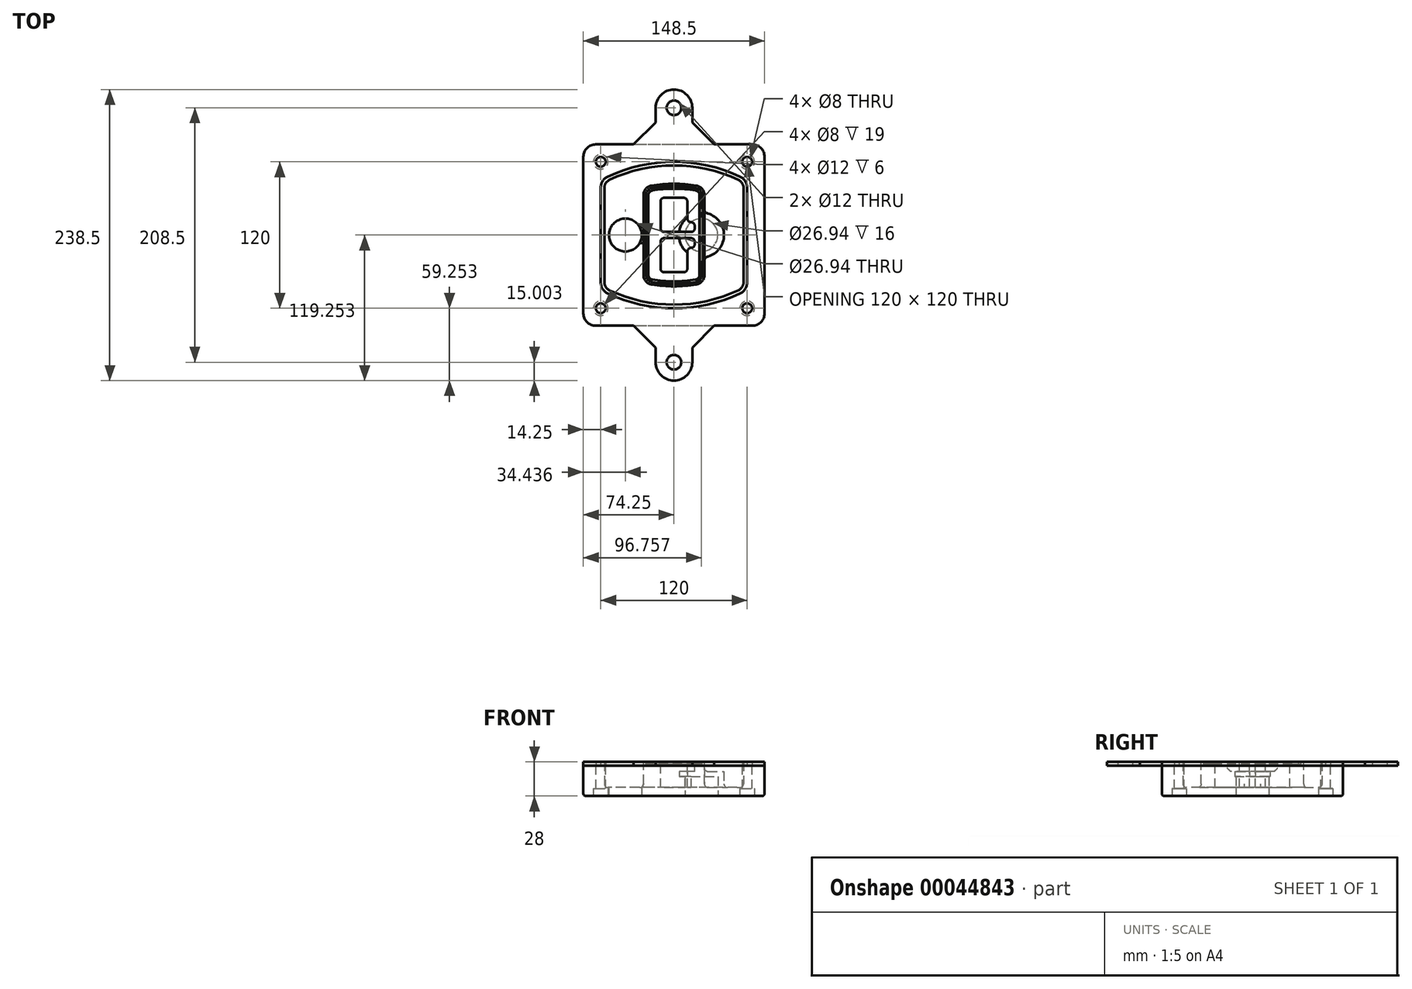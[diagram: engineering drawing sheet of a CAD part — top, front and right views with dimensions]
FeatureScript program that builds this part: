
annotation { "Feature Type Name" : "Feature", "Feature Type Description" : "" }
export const myFeature = defineFeature(function(context is Context, id is Id, definition is map)
    precondition{}
    {
        {
            var Q0;
            Q0=qCreatedBy(makeId("Top.planeOp"),FACE);
            var sketch = newSketch(context, id + "F0", { "sketchPlane" : qUnion([Q0])});
            skPoint(sketch, "E0.rect.middle", {"position": v(0, 0) * mm});
            skLineSegment(sketch, "E1.bottom", {"start": v(24.05, 28.38) * mm, "end": v(152.55, 28.38) * mm});
            skLineSegment(sketch, "E1.top", {"start": v(24.05, 176.88) * mm, "end": v(152.55, 176.88) * mm});
            skLineSegment(sketch, "E1.left", {"start": v(14.05, 38.38) * mm, "end": v(14.05, 166.88) * mm});
            skLineSegment(sketch, "E1.right", {"start": v(162.55, 38.38) * mm, "end": v(162.55, 166.88) * mm});
            skLineSegment(sketch, "E2", {"start": v(14.05, 176.88) * mm, "end": v(162.55, 28.38) * mm, "construction": true});
            skLineSegment(sketch, "E3", {"start": v(162.55, 176.88) * mm, "end": v(14.05, 28.38) * mm, "construction": true});
            skCircle(sketch, "E4", {"center": v(28.3, 162.63) * mm, "radius": 4 * mm});
            skCircle(sketch, "E5", {"center": v(148.3, 162.63) * mm, "radius": 4 * mm});
            skCircle(sketch, "E6", {"center": v(148.3, 42.63) * mm, "radius": 4 * mm});
            skCircle(sketch, "E7", {"center": v(28.3, 42.63) * mm, "radius": 4 * mm});
            skLineSegment(sketch, "E8", {"start": v(28.3, 162.63) * mm, "end": v(148.3, 162.63) * mm, "construction": true});
            skLineSegment(sketch, "E9", {"start": v(148.3, 162.63) * mm, "end": v(148.3, 42.63) * mm, "construction": true});
            skLineSegment(sketch, "E10", {"start": v(148.3, 42.63) * mm, "end": v(28.3, 42.63) * mm, "construction": true});
            skLineSegment(sketch, "E11", {"start": v(28.3, 42.63) * mm, "end": v(28.3, 162.63) * mm, "construction": true});
            skLineSegment(sketch, "E12", {"start": v(28.3, 141.46) * mm, "end": v(28.3, 63.8) * mm});
            skLineSegment(sketch, "E13", {"start": v(148.3, 141.46) * mm, "end": v(148.3, 63.8) * mm});
            skArc(sketch, "E14", {"start": v(142.56, 150.51) * mm, "mid": v(88.3, 162.63) * mm, "end": v(34.04, 150.51) * mm});
            skArc(sketch, "E15", {"start": v(34.04, 54.75) * mm, "mid": v(88.3, 42.63) * mm, "end": v(142.56, 54.75) * mm});
            skLineSegment(sketch, "E16", {"start": v(28.3, 102.63) * mm, "end": v(148.3, 102.63) * mm, "construction": true});
            skPoint(sketch, "E17.visualSharp", {"position": v(28.3, 57.63) * mm});
            skArc(sketch, "E17.filletArc", {"start": v(28.3, 63.8) * mm, "mid": v(29.86, 58.44) * mm, "end": v(34.04, 54.75) * mm});
            skPoint(sketch, "E18.visualSharp", {"position": v(28.3, 147.63) * mm});
            skArc(sketch, "E18.filletArc", {"start": v(34.04, 150.51) * mm, "mid": v(29.86, 146.82) * mm, "end": v(28.3, 141.46) * mm});
            skPoint(sketch, "E19.visualSharp", {"position": v(148.3, 147.63) * mm});
            skArc(sketch, "E19.filletArc", {"start": v(148.3, 141.46) * mm, "mid": v(146.74, 146.82) * mm, "end": v(142.56, 150.51) * mm});
            skPoint(sketch, "E20.visualSharp", {"position": v(148.3, 57.63) * mm});
            skArc(sketch, "E20.filletArc", {"start": v(142.56, 54.75) * mm, "mid": v(146.74, 58.44) * mm, "end": v(148.3, 63.8) * mm});
            skPoint(sketch, "E21.visualSharp", {"position": v(14.05, 176.88) * mm});
            skArc(sketch, "E21.filletArc", {"start": v(24.05, 176.88) * mm, "mid": v(16.98, 173.95) * mm, "end": v(14.05, 166.88) * mm});
            skPoint(sketch, "E22.visualSharp", {"position": v(162.55, 176.88) * mm});
            skArc(sketch, "E22.filletArc", {"start": v(162.55, 166.88) * mm, "mid": v(159.62, 173.95) * mm, "end": v(152.55, 176.88) * mm});
            skPoint(sketch, "E23.visualSharp", {"position": v(162.55, 28.38) * mm});
            skArc(sketch, "E23.filletArc", {"start": v(152.55, 28.38) * mm, "mid": v(159.62, 31.31) * mm, "end": v(162.55, 38.38) * mm});
            skPoint(sketch, "E24.visualSharp", {"position": v(14.05, 28.38) * mm});
            skArc(sketch, "E24.filletArc", {"start": v(14.05, 38.38) * mm, "mid": v(16.98, 31.31) * mm, "end": v(24.05, 28.38) * mm});
            skArc(sketch, "E25.0", {"start": v(145.3, 141.46) * mm, "mid": v(144.2, 145.22) * mm, "end": v(141.28, 147.8) * mm});
            skLineSegment(sketch, "E25.1", {"start": v(145.3, 141.46) * mm, "end": v(145.3, 63.8) * mm});
            skArc(sketch, "E25.2", {"start": v(141.28, 57.47) * mm, "mid": v(144.2, 60.05) * mm, "end": v(145.3, 63.8) * mm});
            skArc(sketch, "E25.3", {"start": v(35.32, 57.47) * mm, "mid": v(88.3, 45.63) * mm, "end": v(141.28, 57.47) * mm});
            skArc(sketch, "E25.4", {"start": v(31.3, 63.8) * mm, "mid": v(32.4, 60.05) * mm, "end": v(35.32, 57.47) * mm});
            skArc(sketch, "E25.5", {"start": v(141.28, 147.8) * mm, "mid": v(88.3, 159.63) * mm, "end": v(35.32, 147.8) * mm});
            skLineSegment(sketch, "E25.6", {"start": v(31.3, 141.46) * mm, "end": v(31.3, 63.8) * mm});
            skArc(sketch, "E25.7", {"start": v(35.32, 147.8) * mm, "mid": v(32.4, 145.22) * mm, "end": v(31.3, 141.46) * mm});
            skArc(sketch, "E26.0", {"start": v(32.34, 154.13) * mm, "mid": v(26.48, 148.97) * mm, "end": v(24.3, 141.46) * mm});
            skArc(sketch, "E26.1", {"start": v(144.26, 154.13) * mm, "mid": v(88.3, 166.63) * mm, "end": v(32.34, 154.13) * mm});
            skArc(sketch, "E26.2", {"start": v(152.3, 141.46) * mm, "mid": v(150.12, 148.97) * mm, "end": v(144.26, 154.13) * mm});
            skLineSegment(sketch, "E26.3", {"start": v(152.3, 141.46) * mm, "end": v(152.3, 63.8) * mm});
            skArc(sketch, "E26.4", {"start": v(144.26, 51.13) * mm, "mid": v(150.12, 56.3) * mm, "end": v(152.3, 63.8) * mm});
            skLineSegment(sketch, "E26.5", {"start": v(24.3, 141.46) * mm, "end": v(24.3, 63.8) * mm});
            skArc(sketch, "E26.6", {"start": v(32.34, 51.13) * mm, "mid": v(88.3, 38.63) * mm, "end": v(144.26, 51.13) * mm});
            skArc(sketch, "E26.7", {"start": v(24.3, 63.8) * mm, "mid": v(26.48, 56.3) * mm, "end": v(32.34, 51.13) * mm});
            skSolve(sketch);
        }
        {
            var Q0;
            Q0=makeQuery(id+"F0.imprint","IMPRINT",FACE,{"disambiguationData":[TD([[makeQuery(id+"F0.imprint","IMPRINT",EDGE,{"derivedFrom":sQuery(id+"F0.wireOp",EDGE,"E1.bottom")}),1.0]])]});
            var Q1;
            Q1=makeQuery(id+"F0.imprint","IMPRINT",FACE,{"disambiguationData":[TD([[makeQuery(id+"F0.imprint","IMPRINT",EDGE,{"derivedFrom":sQuery(id+"F0.wireOp",EDGE,"E12")}),1.0]])]});
            var Q2;
            Q2=makeQuery(id+"F0.imprint","IMPRINT",FACE,{"disambiguationData":[TD([[makeQuery(id+"F0.imprint","IMPRINT",EDGE,{"derivedFrom":sQuery(id+"F0.wireOp",EDGE,"E25.0")}),1.0]])]});
            var Q3;
            Q3=makeQuery(id+"F0.imprint","IMPRINT",FACE,{"disambiguationData":[TD([[makeQuery(id+"F0.imprint","IMPRINT",EDGE,{"derivedFrom":sQuery(id+"F0.wireOp",EDGE,"E12")}),-1.0]])]});
            extrude(context, id + "F1", {"entities" : qUnion([Q0, Q1, Q2, Q3]), "oppositeDirection" : true, "depth" : 25 * mm});
        }
        {
            var Q0;
            Q0=makeQuery(id+"F0.imprint","IMPRINT",FACE,{"disambiguationData":[TD([[makeQuery(id+"F0.imprint","IMPRINT",EDGE,{"derivedFrom":sQuery(id+"F0.wireOp",EDGE,"E12")}),1.0]])]});
            extrude(context, id + "F2", {"entities" : qUnion([Q0]), "operationType" : NewBodyOperationType.ADD, "depth" : 3 * mm});
        }
        {
            var Q0;
            Q0=makeQuery(id+"F0.imprint","IMPRINT",FACE,{"disambiguationData":[TD([[makeQuery(id+"F0.imprint","IMPRINT",EDGE,{"derivedFrom":sQuery(id+"F0.wireOp",EDGE,"E25.0")}),1.0]])]});
            extrude(context, id + "F3", {"entities" : qUnion([Q0]), "operationType" : NewBodyOperationType.REMOVE, "oppositeDirection" : true, "depth" : 18 * mm});
        }
        {
            var Q0;
            Q0=makeQuery(id+"F2.opExtrude","CAP_FACE",FACE,{"disambiguationData":[OSD([sQuery(id+"F0.wireOp",EDGE,"E12"),sQuery(id+"F0.wireOp",EDGE,"E13"),sQuery(id+"F0.wireOp",EDGE,"E14"),sQuery(id+"F0.wireOp",EDGE,"E15"),sQuery(id+"F0.wireOp",EDGE,"E17.filletArc"),sQuery(id+"F0.wireOp",EDGE,"E18.filletArc"),sQuery(id+"F0.wireOp",EDGE,"E19.filletArc"),sQuery(id+"F0.wireOp",EDGE,"E20.filletArc"),sQuery(id+"F0.wireOp",EDGE,"E25.0"),sQuery(id+"F0.wireOp",EDGE,"E25.1"),sQuery(id+"F0.wireOp",EDGE,"E25.2"),sQuery(id+"F0.wireOp",EDGE,"E25.3"),sQuery(id+"F0.wireOp",EDGE,"E25.4"),sQuery(id+"F0.wireOp",EDGE,"E25.5"),sQuery(id+"F0.wireOp",EDGE,"E25.6"),sQuery(id+"F0.wireOp",EDGE,"E25.7")])],"isStart":false});
            var sketch = newSketch(context, id + "F4", { "sketchPlane" : qUnion([Q0])});
            skArc(sketch, "E27.0", {"start": v(69.96, 62.18) * mm, "mid": v(88.3, 60.63) * mm, "end": v(106.64, 62.18) * mm});
            skArc(sketch, "E28.0", {"start": v(106.64, 143.09) * mm, "mid": v(88.3, 144.63) * mm, "end": v(69.96, 143.09) * mm});
            skLineSegment(sketch, "E29", {"start": v(63.3, 135.2) * mm, "end": v(63.3, 70.07) * mm});
            skLineSegment(sketch, "E30", {"start": v(113.3, 135.2) * mm, "end": v(113.3, 70.07) * mm});
            skLineSegment(sketch, "E31", {"start": v(63.3, 141.74) * mm, "end": v(113.3, 141.74) * mm, "construction": true});
            skLineSegment(sketch, "E32", {"start": v(63.3, 63.52) * mm, "end": v(113.3, 63.52) * mm, "construction": true});
            skPoint(sketch, "E33.visualSharp", {"position": v(63.3, 141.74) * mm});
            skArc(sketch, "E33.filletArc", {"start": v(69.96, 143.09) * mm, "mid": v(65.19, 140.36) * mm, "end": v(63.3, 135.2) * mm});
            skPoint(sketch, "E34.visualSharp", {"position": v(113.3, 141.74) * mm});
            skArc(sketch, "E34.filletArc", {"start": v(113.3, 135.2) * mm, "mid": v(111.41, 140.36) * mm, "end": v(106.64, 143.09) * mm});
            skPoint(sketch, "E35.visualSharp", {"position": v(113.3, 63.52) * mm});
            skArc(sketch, "E35.filletArc", {"start": v(106.64, 62.18) * mm, "mid": v(111.41, 64.9) * mm, "end": v(113.3, 70.07) * mm});
            skPoint(sketch, "E36.visualSharp", {"position": v(63.3, 63.52) * mm});
            skArc(sketch, "E36.filletArc", {"start": v(63.3, 70.07) * mm, "mid": v(65.19, 64.9) * mm, "end": v(69.96, 62.18) * mm});
            skArc(sketch, "E37.0", {"start": v(141.28, 147.8) * mm, "mid": v(88.3, 159.63) * mm, "end": v(35.32, 147.8) * mm});
            skArc(sketch, "E37.1", {"start": v(35.32, 147.8) * mm, "mid": v(32.4, 145.22) * mm, "end": v(31.3, 141.46) * mm});
            skLineSegment(sketch, "E37.2", {"start": v(31.3, 141.46) * mm, "end": v(31.3, 63.8) * mm});
            skArc(sketch, "E37.3", {"start": v(31.3, 63.8) * mm, "mid": v(32.4, 60.05) * mm, "end": v(35.32, 57.47) * mm});
            skArc(sketch, "E37.4", {"start": v(35.32, 57.47) * mm, "mid": v(88.3, 45.63) * mm, "end": v(141.28, 57.47) * mm});
            skArc(sketch, "E37.5", {"start": v(141.28, 57.47) * mm, "mid": v(144.2, 60.05) * mm, "end": v(145.3, 63.8) * mm});
            skLineSegment(sketch, "E37.6", {"start": v(145.3, 141.46) * mm, "end": v(145.3, 63.8) * mm});
            skArc(sketch, "E37.7", {"start": v(145.3, 141.46) * mm, "mid": v(144.2, 145.22) * mm, "end": v(141.28, 147.8) * mm});
            skLineSegment(sketch, "E38.0", {"start": v(111.3, 135.2) * mm, "end": v(111.3, 70.07) * mm});
            skArc(sketch, "E38.1", {"start": v(106.3, 64.15) * mm, "mid": v(109.88, 66.2) * mm, "end": v(111.3, 70.07) * mm});
            skArc(sketch, "E38.2", {"start": v(70.3, 64.15) * mm, "mid": v(88.3, 62.63) * mm, "end": v(106.3, 64.15) * mm});
            skArc(sketch, "E38.3", {"start": v(65.3, 70.07) * mm, "mid": v(66.72, 66.2) * mm, "end": v(70.3, 64.15) * mm});
            skLineSegment(sketch, "E38.4", {"start": v(65.3, 135.2) * mm, "end": v(65.3, 70.07) * mm});
            skArc(sketch, "E38.5", {"start": v(111.3, 135.2) * mm, "mid": v(109.88, 139.07) * mm, "end": v(106.3, 141.11) * mm});
            skArc(sketch, "E38.6", {"start": v(70.3, 141.11) * mm, "mid": v(66.72, 139.07) * mm, "end": v(65.3, 135.2) * mm});
            skArc(sketch, "E38.7", {"start": v(106.3, 141.11) * mm, "mid": v(88.3, 142.63) * mm, "end": v(70.3, 141.11) * mm});
            skArc(sketch, "E39.0", {"start": v(109.3, 135.2) * mm, "mid": v(108.36, 137.78) * mm, "end": v(105.97, 139.14) * mm});
            skLineSegment(sketch, "E39.1", {"start": v(109.3, 135.2) * mm, "end": v(109.3, 70.07) * mm});
            skArc(sketch, "E39.2", {"start": v(105.97, 66.12) * mm, "mid": v(108.36, 67.49) * mm, "end": v(109.3, 70.07) * mm});
            skArc(sketch, "E39.3", {"start": v(70.63, 66.12) * mm, "mid": v(88.3, 64.63) * mm, "end": v(105.97, 66.12) * mm});
            skArc(sketch, "E39.4", {"start": v(67.3, 70.07) * mm, "mid": v(68.24, 67.49) * mm, "end": v(70.63, 66.12) * mm});
            skArc(sketch, "E39.5", {"start": v(105.97, 139.14) * mm, "mid": v(88.3, 140.63) * mm, "end": v(70.63, 139.14) * mm});
            skLineSegment(sketch, "E39.6", {"start": v(67.3, 135.2) * mm, "end": v(67.3, 70.07) * mm});
            skArc(sketch, "E39.7", {"start": v(70.63, 139.14) * mm, "mid": v(68.24, 137.78) * mm, "end": v(67.3, 135.2) * mm});
            skLineSegment(sketch, "E40", {"start": v(63.3, 102.63) * mm, "end": v(113.3, 102.63) * mm, "construction": true});
            skLineSegment(sketch, "E41", {"start": v(77.3, 108.13) * mm, "end": v(77.3, 130.13) * mm});
            skLineSegment(sketch, "E42", {"start": v(80.3, 133.13) * mm, "end": v(96.3, 133.13) * mm});
            skLineSegment(sketch, "E43", {"start": v(99.3, 130.13) * mm, "end": v(99.3, 116.13) * mm});
            skLineSegment(sketch, "E44", {"start": v(102.3, 113.13) * mm, "end": v(102.3, 113.13) * mm});
            skLineSegment(sketch, "E45", {"start": v(105.3, 110.13) * mm, "end": v(105.3, 108.13) * mm});
            skLineSegment(sketch, "E46", {"start": v(102.3, 105.13) * mm, "end": v(80.3, 105.13) * mm});
            skPoint(sketch, "E47.visualSharp", {"position": v(77.3, 133.13) * mm});
            skArc(sketch, "E47.filletArc", {"start": v(80.3, 133.13) * mm, "mid": v(78.18, 132.25) * mm, "end": v(77.3, 130.13) * mm});
            skPoint(sketch, "E48.visualSharp", {"position": v(99.3, 133.13) * mm});
            skArc(sketch, "E48.filletArc", {"start": v(99.3, 130.13) * mm, "mid": v(98.42, 132.25) * mm, "end": v(96.3, 133.13) * mm});
            skPoint(sketch, "E49.visualSharp", {"position": v(99.3, 113.13) * mm});
            skArc(sketch, "E49.filletArc", {"start": v(99.3, 116.13) * mm, "mid": v(100.18, 114.01) * mm, "end": v(102.3, 113.13) * mm});
            skPoint(sketch, "E50.visualSharp", {"position": v(105.3, 113.13) * mm});
            skArc(sketch, "E50.filletArc", {"start": v(105.3, 110.13) * mm, "mid": v(104.42, 112.25) * mm, "end": v(102.3, 113.13) * mm});
            skPoint(sketch, "E51.visualSharp", {"position": v(105.3, 105.13) * mm});
            skArc(sketch, "E51.filletArc", {"start": v(102.3, 105.13) * mm, "mid": v(104.42, 106.01) * mm, "end": v(105.3, 108.13) * mm});
            skPoint(sketch, "E52.visualSharp", {"position": v(77.3, 105.13) * mm});
            skArc(sketch, "E52.filletArc", {"start": v(77.3, 108.13) * mm, "mid": v(78.18, 106.01) * mm, "end": v(80.3, 105.13) * mm});
            skLineSegment(sketch, "E53.0.MirrorCS", {"start": v(102.3, 100.13) * mm, "end": v(80.3, 100.13) * mm});
            skArc(sketch, "E54.0.MirrorCS", {"start": v(77.3, 97.13) * mm, "mid": v(78.18, 99.25) * mm, "end": v(80.3, 100.13) * mm});
            skLineSegment(sketch, "E55.0.MirrorCS", {"start": v(77.3, 97.13) * mm, "end": v(77.3, 75.13) * mm});
            skArc(sketch, "E56.0.MirrorCS", {"start": v(80.3, 72.13) * mm, "mid": v(78.18, 73.01) * mm, "end": v(77.3, 75.13) * mm});
            skLineSegment(sketch, "E57.0.MirrorCS", {"start": v(80.3, 72.13) * mm, "end": v(96.3, 72.13) * mm});
            skArc(sketch, "E58.0.MirrorCS", {"start": v(99.3, 75.13) * mm, "mid": v(98.42, 73.01) * mm, "end": v(96.3, 72.13) * mm});
            skLineSegment(sketch, "E59.0.MirrorCS", {"start": v(99.3, 75.13) * mm, "end": v(99.3, 89.13) * mm});
            skArc(sketch, "E60.0.MirrorCS", {"start": v(99.3, 89.13) * mm, "mid": v(100.18, 91.25) * mm, "end": v(102.3, 92.13) * mm});
            skArc(sketch, "E61.0.MirrorCS", {"start": v(105.3, 95.13) * mm, "mid": v(104.42, 93.01) * mm, "end": v(102.3, 92.13) * mm});
            skLineSegment(sketch, "E62.0.MirrorCS", {"start": v(105.3, 95.13) * mm, "end": v(105.3, 97.13) * mm});
            skArc(sketch, "E63.0.MirrorCS", {"start": v(102.3, 100.13) * mm, "mid": v(104.42, 99.25) * mm, "end": v(105.3, 97.13) * mm});
            skSolve(sketch);
        }
        {
            var Q0;
            Q0=makeQuery(id+"F4.imprint","IMPRINT",FACE,{"disambiguationData":[TD([[makeQuery(id+"F4.imprint","IMPRINT",EDGE,{"derivedFrom":sQuery(id+"F4.wireOp",EDGE,"E27.0")}),1.0]])]});
            var Q1;
            Q1=makeQuery(id+"F4.imprint","IMPRINT",FACE,{"disambiguationData":[TD([[makeQuery(id+"F4.imprint","IMPRINT",EDGE,{"derivedFrom":sQuery(id+"F4.wireOp",EDGE,"E38.0")}),-1.0]])]});
            var Q2;
            Q2=makeQuery(id+"F4.imprint","IMPRINT",FACE,{"disambiguationData":[TD([[makeQuery(id+"F4.imprint","IMPRINT",EDGE,{"derivedFrom":sQuery(id+"F4.wireOp",EDGE,"E39.0")}),1.0]])]});
            extrude(context, id + "F5", {"entities" : qUnion([Q0, Q1, Q2]), "operationType" : NewBodyOperationType.ADD, "endBound" : BoundingType.UP_TO_NEXT, "oppositeDirection" : true, "depth" : 25 * mm});
        }
        {
            var Q0;
            Q0=makeQuery(id+"F4.imprint","IMPRINT",FACE,{"disambiguationData":[TD([[makeQuery(id+"F4.imprint","IMPRINT",EDGE,{"derivedFrom":sQuery(id+"F4.wireOp",EDGE,"E38.0")}),-1.0]])]});
            extrude(context, id + "F6", {"entities" : qUnion([Q0]), "operationType" : NewBodyOperationType.REMOVE, "oppositeDirection" : true, "depth" : 2 * mm});
        }
        {
            var Q0;
            Q0=makeQuery(id+"F1.opExtrude","CAP_FACE",FACE,{"disambiguationData":[OSD([sQuery(id+"F0.wireOp",EDGE,"E1.bottom"),sQuery(id+"F0.wireOp",EDGE,"E1.top"),sQuery(id+"F0.wireOp",EDGE,"E1.left"),sQuery(id+"F0.wireOp",EDGE,"E1.right"),sQuery(id+"F0.wireOp",EDGE,"E4"),sQuery(id+"F0.wireOp",EDGE,"E5"),sQuery(id+"F0.wireOp",EDGE,"E6"),sQuery(id+"F0.wireOp",EDGE,"E7"),sQuery(id+"F0.wireOp",EDGE,"E21.filletArc"),sQuery(id+"F0.wireOp",EDGE,"E22.filletArc"),sQuery(id+"F0.wireOp",EDGE,"E23.filletArc"),sQuery(id+"F0.wireOp",EDGE,"E24.filletArc")])],"isStart":false});
            var sketch = newSketch(context, id + "F7", { "sketchPlane" : qUnion([Q0])});
            skCircle(sketch, "E64", {"center": v(110.8, -102.63) * mm, "radius": 13.47 * mm});
            skCircle(sketch, "E65", {"center": v(48.49, -102.63) * mm, "radius": 13.47 * mm});
            skLineSegment(sketch, "E66", {"start": v(162.55, -102.63) * mm, "end": v(14.05, -102.63) * mm});
            skCircle(sketch, "E67", {"center": v(110.8, -102.63) * mm, "radius": 18.47 * mm});
            skCircle(sketch, "E68", {"center": v(148.3, -162.63) * mm, "radius": 6 * mm});
            skCircle(sketch, "E69", {"center": v(28.3, -162.63) * mm, "radius": 6 * mm});
            skCircle(sketch, "E70", {"center": v(28.3, -42.63) * mm, "radius": 6 * mm});
            skCircle(sketch, "E71", {"center": v(148.3, -42.63) * mm, "radius": 6 * mm});
            skSolve(sketch);
        }
        {
            var Q0;
            {var subQ1=sQuery(id+"F7.wireOp",EDGE,"E66");var subQ4=sQuery(id+"F7.wireOp",EDGE,"E64");var subQ6=makeQuery(id+"F7.imprint","INTERSECT",VERTEX,{"disambiguationData":[OD(0.0)],"derivedFrom":[subQ4,subQ1]});Q0=makeQuery(id+"F7.imprint","IMPRINT",FACE,{"disambiguationData":[TD([[makeQuery(id+"F7.imprint","IMPRINT",EDGE,{"disambiguationData":[TD([[subQ6,-1.0]])],"derivedFrom":subQ4}),-1.0]])]});}
            var Q1;
            {var subQ0=sQuery(id+"F7.wireOp",EDGE,"E66");var subQ1=sQuery(id+"F7.wireOp",EDGE,"E64");var subQ3=makeQuery(id+"F7.imprint","INTERSECT",VERTEX,{"disambiguationData":[OD(0.0)],"derivedFrom":[subQ1,subQ0]});Q1=makeQuery(id+"F7.imprint","IMPRINT",FACE,{"disambiguationData":[TD([[makeQuery(id+"F7.imprint","IMPRINT",EDGE,{"disambiguationData":[TD([[subQ3,-1.0]])],"derivedFrom":subQ1}),1.0]])]});}
            var Q2;
            {var subQ0=sQuery(id+"F7.wireOp",EDGE,"E66");var subQ1=sQuery(id+"F7.wireOp",EDGE,"E64");var subQ3=makeQuery(id+"F7.imprint","INTERSECT",VERTEX,{"disambiguationData":[OD(0.0)],"derivedFrom":[subQ1,subQ0]});Q2=makeQuery(id+"F7.imprint","IMPRINT",FACE,{"disambiguationData":[TD([[makeQuery(id+"F7.imprint","IMPRINT",EDGE,{"disambiguationData":[TD([[subQ3,1.0]])],"derivedFrom":subQ1}),1.0]])]});}
            var Q3;
            {var subQ1=sQuery(id+"F7.wireOp",EDGE,"E66");var subQ4=sQuery(id+"F7.wireOp",EDGE,"E64");var subQ6=makeQuery(id+"F7.imprint","INTERSECT",VERTEX,{"disambiguationData":[OD(0.0)],"derivedFrom":[subQ4,subQ1]});Q3=makeQuery(id+"F7.imprint","IMPRINT",FACE,{"disambiguationData":[TD([[makeQuery(id+"F7.imprint","IMPRINT",EDGE,{"disambiguationData":[TD([[subQ6,1.0]])],"derivedFrom":subQ4}),-1.0]])]});}
            extrude(context, id + "F8", {"entities" : qUnion([Q0, Q1, Q2, Q3]), "operationType" : NewBodyOperationType.ADD, "oppositeDirection" : true, "depth" : 20 * mm});
        }
        {
            var Q0;
            {var subQ0=sQuery(id+"F7.wireOp",EDGE,"E66");var subQ1=sQuery(id+"F7.wireOp",EDGE,"E64");var subQ3=makeQuery(id+"F7.imprint","INTERSECT",VERTEX,{"disambiguationData":[OD(0.0)],"derivedFrom":[subQ1,subQ0]});Q0=makeQuery(id+"F7.imprint","IMPRINT",FACE,{"disambiguationData":[TD([[makeQuery(id+"F7.imprint","IMPRINT",EDGE,{"disambiguationData":[TD([[subQ3,-1.0]])],"derivedFrom":subQ1}),1.0]])]});}
            var Q1;
            {var subQ0=sQuery(id+"F7.wireOp",EDGE,"E66");var subQ1=sQuery(id+"F7.wireOp",EDGE,"E64");var subQ3=makeQuery(id+"F7.imprint","INTERSECT",VERTEX,{"disambiguationData":[OD(0.0)],"derivedFrom":[subQ1,subQ0]});Q1=makeQuery(id+"F7.imprint","IMPRINT",FACE,{"disambiguationData":[TD([[makeQuery(id+"F7.imprint","IMPRINT",EDGE,{"disambiguationData":[TD([[subQ3,1.0]])],"derivedFrom":subQ1}),1.0]])]});}
            extrude(context, id + "F9", {"entities" : qUnion([Q0, Q1]), "operationType" : NewBodyOperationType.REMOVE, "oppositeDirection" : true, "depth" : 16 * mm});
        }
        {
            var Q0;
            {var subQ0=sQuery(id+"F7.wireOp",EDGE,"E66");var subQ1=sQuery(id+"F7.wireOp",EDGE,"E65");var subQ3=makeQuery(id+"F7.imprint","INTERSECT",VERTEX,{"disambiguationData":[OD(0.0)],"derivedFrom":[subQ1,subQ0]});Q0=makeQuery(id+"F7.imprint","IMPRINT",FACE,{"disambiguationData":[TD([[makeQuery(id+"F7.imprint","IMPRINT",EDGE,{"disambiguationData":[TD([[subQ3,-1.0]])],"derivedFrom":subQ1}),1.0]])]});}
            var Q1;
            {var subQ0=sQuery(id+"F7.wireOp",EDGE,"E66");var subQ1=sQuery(id+"F7.wireOp",EDGE,"E65");var subQ3=makeQuery(id+"F7.imprint","INTERSECT",VERTEX,{"disambiguationData":[OD(0.0)],"derivedFrom":[subQ1,subQ0]});Q1=makeQuery(id+"F7.imprint","IMPRINT",FACE,{"disambiguationData":[TD([[makeQuery(id+"F7.imprint","IMPRINT",EDGE,{"disambiguationData":[TD([[subQ3,1.0]])],"derivedFrom":subQ1}),1.0]])]});}
            extrude(context, id + "F10", {"entities" : qUnion([Q0, Q1]), "operationType" : NewBodyOperationType.REMOVE, "oppositeDirection" : true, "depth" : 25 * mm});
        }
        {
            var Q0;
            Q0=makeQuery(id+"F7.imprint","IMPRINT",FACE,{"disambiguationData":[TD([[makeQuery(id+"F7.imprint","IMPRINT",EDGE,{"derivedFrom":sQuery(id+"F7.wireOp",EDGE,"E68")}),1.0]])]});
            var Q1;
            Q1=makeQuery(id+"F7.imprint","IMPRINT",FACE,{"disambiguationData":[TD([[makeQuery(id+"F7.imprint","IMPRINT",EDGE,{"derivedFrom":makeQuery(id+"F1.opExtrude","CAP_EDGE",EDGE,{"disambiguationData":[OSD([sQuery(id+"F0.wireOp",EDGE,"E5")])],"isStart":false})}),-1.0]])]});
            var Q2;
            Q2=makeQuery(id+"F7.imprint","IMPRINT",FACE,{"disambiguationData":[TD([[makeQuery(id+"F7.imprint","IMPRINT",EDGE,{"derivedFrom":sQuery(id+"F7.wireOp",EDGE,"E69")}),1.0]])]});
            var Q3;
            Q3=makeQuery(id+"F7.imprint","IMPRINT",FACE,{"disambiguationData":[TD([[makeQuery(id+"F7.imprint","IMPRINT",EDGE,{"derivedFrom":makeQuery(id+"F1.opExtrude","CAP_EDGE",EDGE,{"disambiguationData":[OSD([sQuery(id+"F0.wireOp",EDGE,"E4")])],"isStart":false})}),-1.0]])]});
            var Q4;
            Q4=makeQuery(id+"F7.imprint","IMPRINT",FACE,{"disambiguationData":[TD([[makeQuery(id+"F7.imprint","IMPRINT",EDGE,{"derivedFrom":sQuery(id+"F7.wireOp",EDGE,"E70")}),1.0]])]});
            var Q5;
            Q5=makeQuery(id+"F7.imprint","IMPRINT",FACE,{"disambiguationData":[TD([[makeQuery(id+"F7.imprint","IMPRINT",EDGE,{"derivedFrom":makeQuery(id+"F1.opExtrude","CAP_EDGE",EDGE,{"disambiguationData":[OSD([sQuery(id+"F0.wireOp",EDGE,"E7")])],"isStart":false})}),-1.0]])]});
            var Q6;
            Q6=makeQuery(id+"F7.imprint","IMPRINT",FACE,{"disambiguationData":[TD([[makeQuery(id+"F7.imprint","IMPRINT",EDGE,{"derivedFrom":sQuery(id+"F7.wireOp",EDGE,"E71")}),1.0]])]});
            var Q7;
            Q7=makeQuery(id+"F7.imprint","IMPRINT",FACE,{"disambiguationData":[TD([[makeQuery(id+"F7.imprint","IMPRINT",EDGE,{"derivedFrom":makeQuery(id+"F1.opExtrude","CAP_EDGE",EDGE,{"disambiguationData":[OSD([sQuery(id+"F0.wireOp",EDGE,"E6")])],"isStart":false})}),-1.0]])]});
            extrude(context, id + "F11", {"entities" : qUnion([Q0, Q1, Q2, Q3, Q4, Q5, Q6, Q7]), "operationType" : NewBodyOperationType.REMOVE, "oppositeDirection" : true, "depth" : 6 * mm});
        }
        {
            var Q0;
            Q0=makeQuery(id+"F9.boolean.opBoolean","COPY",FACE,{"derivedFrom":makeQuery(id+"F9.opExtrude","CAP_FACE",FACE,{"disambiguationData":[OSD([sQuery(id+"F7.wireOp",EDGE,"E64")])],"isStart":false})});
            var sketch = newSketch(context, id + "F12", { "sketchPlane" : qUnion([Q0])});
            skArc(sketch, "E72.0", {"start": v(99.3, -88.19) * mm, "mid": v(94.75, -93.5) * mm, "end": v(92.5, -100.13) * mm});
            skArc(sketch, "E72.1", {"start": v(92.5, -105.13) * mm, "mid": v(94.75, -111.76) * mm, "end": v(99.3, -117.08) * mm});
            skLineSegment(sketch, "E73", {"start": v(92.5, -105.13) * mm, "end": v(102.3, -105.13) * mm});
            skLineSegment(sketch, "E74.0", {"start": v(102.3, -100.13) * mm, "end": v(92.5, -100.13) * mm});
            skArc(sketch, "E74.1", {"start": v(102.3, -100.13) * mm, "mid": v(104.42, -99.25) * mm, "end": v(105.3, -97.13) * mm});
            skLineSegment(sketch, "E74.2", {"start": v(105.3, -95.13) * mm, "end": v(105.3, -97.13) * mm});
            skArc(sketch, "E74.3", {"start": v(105.3, -95.13) * mm, "mid": v(104.42, -93.01) * mm, "end": v(102.3, -92.13) * mm});
            skArc(sketch, "E74.4", {"start": v(99.3, -89.13) * mm, "mid": v(100.18, -91.25) * mm, "end": v(102.3, -92.13) * mm});
            skLineSegment(sketch, "E74.5", {"start": v(99.3, -88.19) * mm, "end": v(99.3, -89.13) * mm});
            skLineSegment(sketch, "E74.7", {"start": v(102.3, -105.13) * mm, "end": v(92.5, -105.13) * mm});
            skArc(sketch, "E74.8", {"start": v(102.3, -105.13) * mm, "mid": v(104.42, -106.01) * mm, "end": v(105.3, -108.13) * mm});
            skLineSegment(sketch, "E74.9", {"start": v(105.3, -110.13) * mm, "end": v(105.3, -108.13) * mm});
            skArc(sketch, "E74.10", {"start": v(105.3, -110.13) * mm, "mid": v(104.42, -112.25) * mm, "end": v(102.3, -113.13) * mm});
            skArc(sketch, "E74.11", {"start": v(99.3, -116.13) * mm, "mid": v(100.18, -114.01) * mm, "end": v(102.3, -113.13) * mm});
            skLineSegment(sketch, "E74.12", {"start": v(99.3, -117.08) * mm, "end": v(99.3, -116.13) * mm});
            skPoint(sketch, "E75.orphan", {"position": v(99.3, -130.13) * mm});
            skPoint(sketch, "E76.orphan", {"position": v(80.3, -105.13) * mm});
            skPoint(sketch, "E77.orphan", {"position": v(80.3, -100.13) * mm});
            skPoint(sketch, "E78.orphan", {"position": v(99.3, -75.13) * mm});
            skSolve(sketch);
        }
        {
            var Q0;
            {var subQ7=sQuery(id+"F12.wireOp",EDGE,"E72.0");var subQ14=sQuery(id+"F12.wireOp",EDGE,"E72.1");var subQ16=sQuery(id+"F12.wireOp",EDGE,"E74.1");var subQ18=sQuery(id+"F12.wireOp",EDGE,"E74.8");Q0=qUnion([makeQuery(id+"F12.imprint","IMPRINT",FACE,{"disambiguationData":[TD([[makeQuery(id+"F12.imprint","IMPRINT",EDGE,{"derivedFrom":subQ7}),1.0]])]}),makeQuery(id+"F12.imprint","IMPRINT",FACE,{"disambiguationData":[TD([[makeQuery(id+"F12.imprint","IMPRINT",EDGE,{"derivedFrom":subQ14}),1.0]])]}),makeQuery(id+"F12.imprint","IMPRINT",FACE,{"disambiguationData":[TD([[makeQuery(id+"F12.imprint","IMPRINT",EDGE,{"derivedFrom":subQ16}),1.0]])]}),makeQuery(id+"F12.imprint","IMPRINT",FACE,{"disambiguationData":[TD([[makeQuery(id+"F12.imprint","IMPRINT",EDGE,{"derivedFrom":subQ18}),-1.0]])]})]);}
            var Q1;
            Q1=makeQuery(id+"F5.boolean.opBoolean","SPLIT",FACE,{"disambiguationData":[TD([makeQuery(id+"F5.opExtrude","SWEPT_FACE",FACE,{"disambiguationData":[OSD([sQuery(id+"F4.wireOp",EDGE,"E41")])]})])],"derivedFrom":makeQuery(id+"F3.boolean.opBoolean","COPY",FACE,{"derivedFrom":makeQuery(id+"F3.opExtrude","CAP_FACE",FACE,{"disambiguationData":[OSD([sQuery(id+"F0.wireOp",EDGE,"E25.0"),sQuery(id+"F0.wireOp",EDGE,"E25.1"),sQuery(id+"F0.wireOp",EDGE,"E25.2"),sQuery(id+"F0.wireOp",EDGE,"E25.3"),sQuery(id+"F0.wireOp",EDGE,"E25.4"),sQuery(id+"F0.wireOp",EDGE,"E25.5"),sQuery(id+"F0.wireOp",EDGE,"E25.6"),sQuery(id+"F0.wireOp",EDGE,"E25.7")])],"isStart":false})})});
            extrude(context, id + "F13", {"entities" : qUnion([Q0]), "operationType" : NewBodyOperationType.REMOVE, "endBound" : BoundingType.UP_TO_SURFACE, "endBoundEntityFace" : qUnion([Q1]), "depth" : 25 * mm});
        }
        {
            var Q0;
            Q0=makeQuery(id+"F3.boolean.opBoolean","COPY",EDGE,{"derivedFrom":makeQuery(id+"F3.opExtrude","CAP_EDGE",EDGE,{"disambiguationData":[OSD([sQuery(id+"F0.wireOp",EDGE,"E25.6")])],"isStart":false})});
            var Q1;
            Q1=makeQuery(id+"F8.boolean.opBoolean","INTERSECT",EDGE,{"derivedFrom":[makeQuery(id+"F5.opExtrude","SWEPT_FACE",FACE,{"disambiguationData":[OSD([sQuery(id+"F4.wireOp",EDGE,"E30")])]}),makeQuery(id+"F8.opExtrude","CAP_FACE",FACE,{"disambiguationData":[OSD([sQuery(id+"F7.wireOp",EDGE,"E67")])],"isStart":false})]});
            var Q2;
            Q2=makeQuery(id+"F8.boolean.opBoolean","INTERSECT",EDGE,{"disambiguationData":[OD(1.0)],"derivedFrom":[makeQuery(id+"F5.opExtrude","SWEPT_FACE",FACE,{"disambiguationData":[OSD([sQuery(id+"F4.wireOp",EDGE,"E30")])]}),makeQuery(id+"F8.opExtrude","SWEPT_FACE",FACE,{"disambiguationData":[OSD([sQuery(id+"F7.wireOp",EDGE,"E67")])]})]});
            var Q3;
            {var subQ0=sQuery(id+"F4.wireOp",EDGE,"E30");Q3=makeQuery(id+"F8.boolean.opBoolean","SPLIT",EDGE,{"disambiguationData":[TD([makeQuery(id+"F5.opExtrude","SWEPT_FACE",FACE,{"disambiguationData":[OSD([sQuery(id+"F4.wireOp",EDGE,"E35.filletArc")])]})])],"derivedFrom":makeQuery(id+"F5.opExtrude","CAP_EDGE",EDGE,{"disambiguationData":[OSD([subQ0])],"isStart":false})});}
            var Q4;
            {var subQ0=sQuery(id+"F0.wireOp",EDGE,"E25.7");var subQ1=sQuery(id+"F0.wireOp",EDGE,"E25.1");var subQ2=sQuery(id+"F0.wireOp",EDGE,"E25.6");var subQ3=sQuery(id+"F0.wireOp",EDGE,"E25.5");var subQ4=sQuery(id+"F0.wireOp",EDGE,"E25.4");var subQ5=sQuery(id+"F0.wireOp",EDGE,"E25.0");var subQ6=sQuery(id+"F0.wireOp",EDGE,"E25.2");var subQ7=sQuery(id+"F0.wireOp",EDGE,"E25.3");Q4=makeQuery(id+"F8.boolean.opBoolean","INTERSECT",EDGE,{"derivedFrom":[makeQuery(id+"F5.boolean.opBoolean","SPLIT",FACE,{"disambiguationData":[TD([makeQuery(id+"F2.opExtrude","SWEPT_FACE",FACE,{"disambiguationData":[OSD([subQ5])]})])],"derivedFrom":makeQuery(id+"F3.boolean.opBoolean","COPY",FACE,{"derivedFrom":makeQuery(id+"F3.opExtrude","CAP_FACE",FACE,{"disambiguationData":[OSD([subQ5,subQ1,subQ6,subQ7,subQ4,subQ3,subQ2,subQ0])],"isStart":false})})}),makeQuery(id+"F8.opExtrude","SWEPT_FACE",FACE,{"disambiguationData":[OSD([sQuery(id+"F7.wireOp",EDGE,"E67")])]})]});}
            var Q5;
            Q5=makeQuery(id+"F8.boolean.opBoolean","INTERSECT",EDGE,{"disambiguationData":[OD(0.0)],"derivedFrom":[makeQuery(id+"F5.opExtrude","SWEPT_FACE",FACE,{"disambiguationData":[OSD([sQuery(id+"F4.wireOp",EDGE,"E30")])]}),makeQuery(id+"F8.opExtrude","SWEPT_FACE",FACE,{"disambiguationData":[OSD([sQuery(id+"F7.wireOp",EDGE,"E67")])]})]});
            fillet(context, id + "F14", {"entities" : qUnion([Q0, Q1, Q2, Q3, Q4, Q5]), "radius" : 3 * mm, "tangentPropagation" : true, "allowEdgeOverflow" : false});
        }
        {
            var Q0;
            Q0=makeQuery(id+"F1.opExtrude","CAP_EDGE",EDGE,{"disambiguationData":[OSD([sQuery(id+"F0.wireOp",EDGE,"E1.bottom")])],"isStart":false});
            fillet(context, id + "F15", {"entities" : qUnion([Q0]), "radius" : 2 * mm, "tangentPropagation" : true, "allowEdgeOverflow" : false});
        }
        {
            var Q0;
            Q0=qCreatedBy(makeId("Top.planeOp"),FACE);
            var sketch = newSketch(context, id + "F16", { "sketchPlane" : qUnion([Q0])});
            skLineSegment(sketch, "E79.0", {"start": v(148.3, 141.46) * mm, "end": v(148.3, 63.8) * mm});
            skArc(sketch, "E79.1", {"start": v(142.56, 54.75) * mm, "mid": v(146.74, 58.44) * mm, "end": v(148.3, 63.8) * mm});
            skArc(sketch, "E79.2", {"start": v(34.04, 54.75) * mm, "mid": v(88.3, 42.63) * mm, "end": v(142.56, 54.75) * mm});
            skArc(sketch, "E79.3", {"start": v(28.3, 63.8) * mm, "mid": v(29.86, 58.44) * mm, "end": v(34.04, 54.75) * mm});
            skLineSegment(sketch, "E79.4", {"start": v(28.3, 141.46) * mm, "end": v(28.3, 63.8) * mm});
            skArc(sketch, "E79.5", {"start": v(34.04, 150.51) * mm, "mid": v(29.86, 146.82) * mm, "end": v(28.3, 141.46) * mm});
            skArc(sketch, "E79.6", {"start": v(142.56, 150.51) * mm, "mid": v(88.3, 162.63) * mm, "end": v(34.04, 150.51) * mm});
            skArc(sketch, "E79.7", {"start": v(148.3, 141.46) * mm, "mid": v(146.74, 146.82) * mm, "end": v(142.56, 150.51) * mm});
            skCircle(sketch, "E79.8", {"center": v(148.3, 162.63) * mm, "radius": 4 * mm});
            skCircle(sketch, "E79.9", {"center": v(148.3, 42.63) * mm, "radius": 4 * mm});
            skCircle(sketch, "E79.10", {"center": v(28.3, 42.63) * mm, "radius": 4 * mm});
            skLineSegment(sketch, "E79.11", {"start": v(14.05, 38.38) * mm, "end": v(14.05, 166.88) * mm});
            skArc(sketch, "E79.12", {"start": v(14.05, 38.38) * mm, "mid": v(16.98, 31.31) * mm, "end": v(24.05, 28.38) * mm});
            skLineSegment(sketch, "E79.13", {"start": v(24.05, 28.38) * mm, "end": v(152.55, 28.38) * mm});
            skArc(sketch, "E79.14", {"start": v(152.55, 28.38) * mm, "mid": v(159.62, 31.31) * mm, "end": v(162.55, 38.38) * mm});
            skLineSegment(sketch, "E79.15", {"start": v(162.55, 38.38) * mm, "end": v(162.55, 166.88) * mm});
            skArc(sketch, "E79.16", {"start": v(162.55, 166.88) * mm, "mid": v(159.62, 173.95) * mm, "end": v(152.55, 176.88) * mm});
            skLineSegment(sketch, "E79.17", {"start": v(24.05, 176.88) * mm, "end": v(152.55, 176.88) * mm});
            skArc(sketch, "E79.18", {"start": v(24.05, 176.88) * mm, "mid": v(16.98, 173.95) * mm, "end": v(14.05, 166.88) * mm});
            skCircle(sketch, "E79.19", {"center": v(28.3, 162.63) * mm, "radius": 4 * mm});
            skLineSegment(sketch, "E80", {"start": v(88.3, 176.88) * mm, "end": v(88.3, 206.88) * mm, "construction": true});
            skCircle(sketch, "E81", {"center": v(88.3, 206.88) * mm, "radius": 6 * mm});
            skArc(sketch, "E82", {"start": v(103.3, 206.88) * mm, "mid": v(88.3, 221.88) * mm, "end": v(73.3, 206.88) * mm});
            skLineSegment(sketch, "E83", {"start": v(73.3, 206.88) * mm, "end": v(73.3, 194.88) * mm});
            skLineSegment(sketch, "E84", {"start": v(103.3, 206.88) * mm, "end": v(103.3, 194.88) * mm});
            skLineSegment(sketch, "E85", {"start": v(73.3, 194.88) * mm, "end": v(55.3, 176.88) * mm});
            skLineSegment(sketch, "E86", {"start": v(103.3, 194.88) * mm, "end": v(121.3, 176.88) * mm});
            skLineSegment(sketch, "E87", {"start": v(14.05, 102.63) * mm, "end": v(162.55, 102.63) * mm, "construction": true});
            skLineSegment(sketch, "E88.MirrorCS", {"start": v(103.3, 10.38) * mm, "end": v(121.3, 28.38) * mm});
            skLineSegment(sketch, "E89.MirrorCS", {"start": v(103.3, -1.62) * mm, "end": v(103.3, 10.38) * mm});
            skArc(sketch, "E90.MirrorCS", {"start": v(103.3, -1.62) * mm, "mid": v(88.3, -16.62) * mm, "end": v(73.3, -1.62) * mm});
            skCircle(sketch, "E91.MirrorC", {"center": v(88.3, -1.62) * mm, "radius": 6 * mm});
            skLineSegment(sketch, "E92.MirrorCS", {"start": v(88.3, 28.38) * mm, "end": v(88.3, -1.62) * mm});
            skLineSegment(sketch, "E93.MirrorCS", {"start": v(73.3, -1.62) * mm, "end": v(73.3, 10.38) * mm});
            skLineSegment(sketch, "E94.MirrorCS", {"start": v(73.3, 10.38) * mm, "end": v(55.3, 28.38) * mm});
            skSolve(sketch);
        }
        {
            var Q0;
            Q0 = qSketchRegion(id + "F16", true);
            var Q1;
            Q1=makeQuery(id+"F2.opExtrude","CAP_FACE",FACE,{"disambiguationData":[OSD([sQuery(id+"F0.wireOp",EDGE,"E12"),sQuery(id+"F0.wireOp",EDGE,"E13"),sQuery(id+"F0.wireOp",EDGE,"E14"),sQuery(id+"F0.wireOp",EDGE,"E15"),sQuery(id+"F0.wireOp",EDGE,"E17.filletArc"),sQuery(id+"F0.wireOp",EDGE,"E18.filletArc"),sQuery(id+"F0.wireOp",EDGE,"E19.filletArc"),sQuery(id+"F0.wireOp",EDGE,"E20.filletArc"),sQuery(id+"F0.wireOp",EDGE,"E25.0"),sQuery(id+"F0.wireOp",EDGE,"E25.1"),sQuery(id+"F0.wireOp",EDGE,"E25.2"),sQuery(id+"F0.wireOp",EDGE,"E25.3"),sQuery(id+"F0.wireOp",EDGE,"E25.4"),sQuery(id+"F0.wireOp",EDGE,"E25.5"),sQuery(id+"F0.wireOp",EDGE,"E25.6"),sQuery(id+"F0.wireOp",EDGE,"E25.7")])],"isStart":false});
            extrude(context, id + "F17", {"entities" : qUnion([Q0]), "endBound" : BoundingType.UP_TO_SURFACE, "endBoundEntityFace" : qUnion([Q1]), "depth" : 25 * mm});
        }
    });
